# Revit family: Electronics_Control-Pads_Biamp_Impera_Echo-8-Button____
name_source: partatom
category: Communication Devices
units: mm (PartAtom-declared; Revit-internal decimal feet)

## family parameters
Cut with Voids When Loaded = Yes
Host = Face
Maintain Annotation Orientation = No
OmniClass Number = 23.85.10.17.11
OmniClass Title = Audio-Visual System Components
Part Type = Normal
Room Calculation Point = No
Round Connector Dimension = Use Diameter
Shared = No

## types (5) — shared parameters
Altitude = 0-6,600 ft (0-2000m) MSL
Apparent Load = 5 VA
Baud Rate = 1200 – 115200 bit/sec
Button Quantity = 8
Button Type = Mechanical
Compliance = CE Marked (Europe), RoHS Directive (Europe)
Connector Description = 12V DC 5W
Data Bits = 7, 8
Default Elevation = 48 "
Description = Impera™ Echo 8-Button Control Pad
Humidity = 10-90% relative humidity (non-condensing)
I/O Quantity = 3
IR Frequency Range = 381 Hz to 500 kHz
LED Indicators = Multi-color
Manufacturer = Biamp
Max Current = 0.5 A
Max Power Consumption = 5 W
Max Voltage = 24 VDC
Model = Impera Echo
Number of Devices Supported Expansion Bus = 2
Number of Poles = 1
Number of Ports RS-232 / IR = 1 (bidirectional), 1 (undirectional)
Output Type = Open drain
Parity = Even, Odd, None
Power Factor = 1
Product Documentation Link = https://downloads.biamp.com
Product Page URL = https://www.biamp.com
Product data url = https://www.bimobject.com
Sense High = > 4 VDC
Sense Low = < 1 VDC
Stop Bits = 1, 1.5, 2
Temperature Range = 32 - 104° F (0 – 40° C)
URL = https://www.biamp.com
Voltage = 12 V
Weight = 0.20 lbf

## per-type parameters (varying)
| type | Depth | Height | Housing Material | KeyPad Height | US | Void Depth | Width | not_US |
| Echo 8USW | 0.9 " | 4.1 " | Biamp - Plastic - White | 2.76 " | Yes | 0.56 " | 1.8 " | No |
| Echo 8DKB | 0.7 " | 1.8 " | Biamp - Plastic - Black | 1.8 " | No | 0.16 " | 2.8 " | Yes |
| Echo 8DKW | 0.7 " | 1.8 " | Biamp - Plastic - White | 1.8 " | No | 0.16 " | 2.8 " | Yes |
| Echo 8EUW | 0.7 " | 2.2 " | Biamp - Plastic - White | 2.2 " | No | 0.16 " | 2.2 " | Yes |
| Echo 8EUB | 0.7 " | 2.2 " | Biamp - Plastic - Black | 2.2 " | No | 0.16 " | 2.2 " | Yes |

## geometry (parser evidence)
native form markers: Sweep x2
no freeform markers — native parametric forms only
